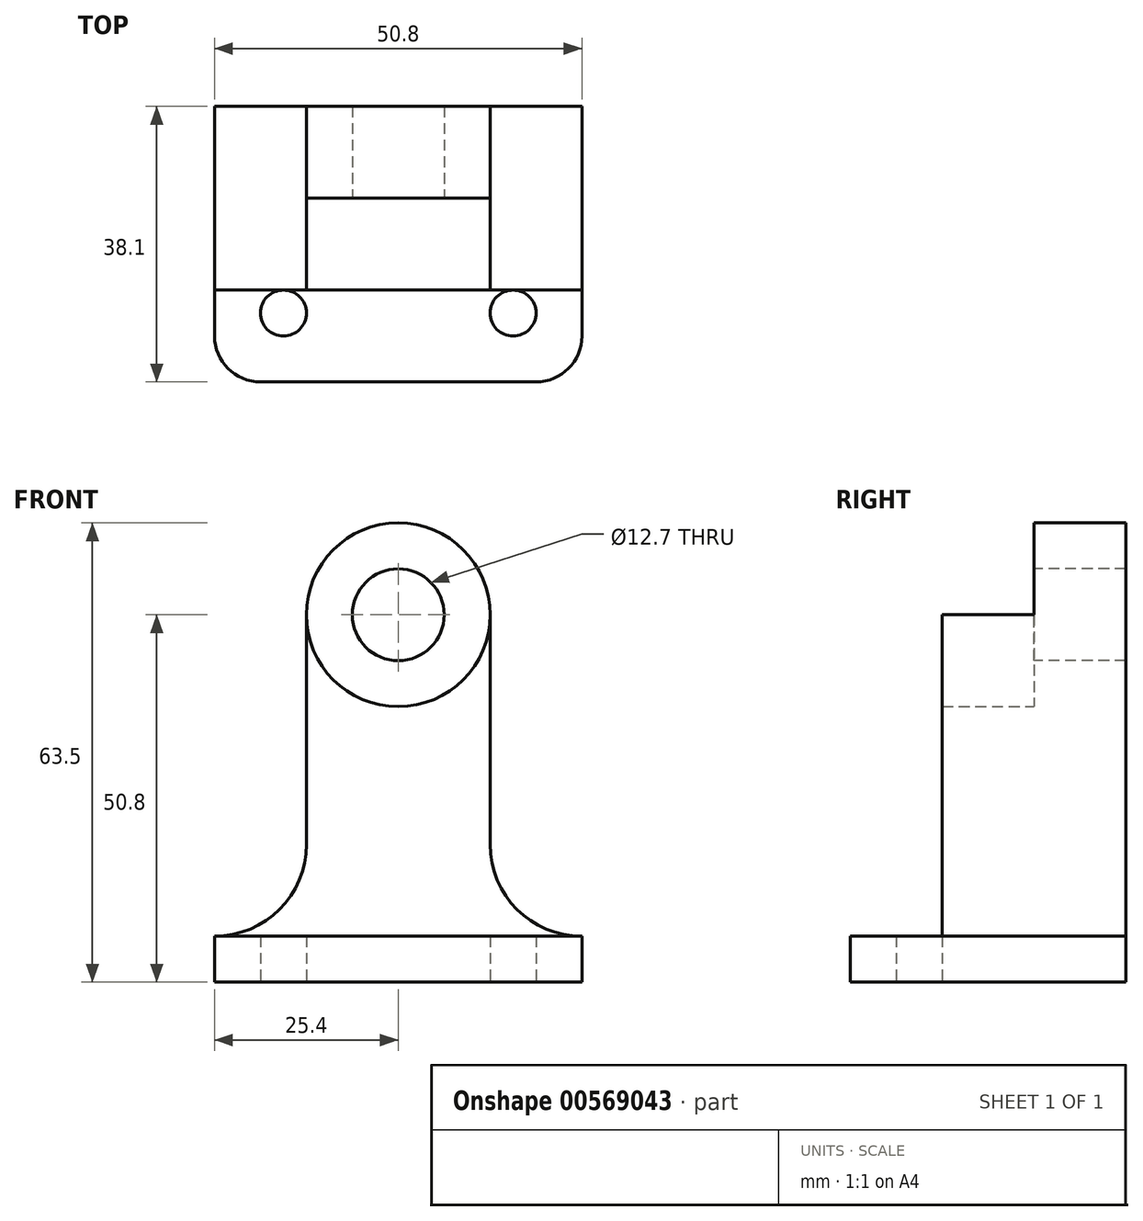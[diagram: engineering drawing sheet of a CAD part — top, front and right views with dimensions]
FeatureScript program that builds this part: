
annotation { "Feature Type Name" : "Feature", "Feature Type Description" : "" }
export const myFeature = defineFeature(function(context is Context, id is Id, definition is map)
    precondition{}
    {
        {
            var Q0;
            Q0=qCreatedBy(makeId("Top.planeOp"),FACE);
            var sketch = newSketch(context, id + "F0", { "sketchPlane" : qUnion([Q0])});
            skLineSegment(sketch, "E0", {"start": v(6.35, 0) * mm, "end": v(44.45, 0) * mm});
            skLineSegment(sketch, "E1", {"start": v(0, 6.35) * mm, "end": v(0, 38.1) * mm});
            skLineSegment(sketch, "E2", {"start": v(0, 38.1) * mm, "end": v(50.8, 38.1) * mm});
            skLineSegment(sketch, "E3", {"start": v(50.8, 38.1) * mm, "end": v(50.8, 6.35) * mm});
            skPoint(sketch, "E4.visualSharp", {"position": v(50.8, 0) * mm});
            skArc(sketch, "E4.filletArc", {"start": v(44.45, 0) * mm, "mid": v(48.94, 1.86) * mm, "end": v(50.8, 6.35) * mm});
            skCircle(sketch, "E5", {"center": v(9.52, 9.53) * mm, "radius": 3.18 * mm});
            skCircle(sketch, "E6", {"center": v(41.28, 9.53) * mm, "radius": 3.18 * mm});
            skPoint(sketch, "E7.visualSharp", {"position": v(0, 0) * mm});
            skArc(sketch, "E7.filletArc", {"start": v(0, 6.35) * mm, "mid": v(1.86, 1.86) * mm, "end": v(6.35, 0) * mm});
            skSolve(sketch);
        }
        {
            var Q0;
            Q0=makeQuery(id+"F0.imprint","IMPRINT",FACE,{"disambiguationData":[TD([[makeQuery(id+"F0.imprint","IMPRINT",EDGE,{"derivedFrom":sQuery(id+"F0.wireOp",EDGE,"E0")}),1.0]])]});
            extrude(context, id + "F1", {"entities" : qUnion([Q0]), "depth" : 6.35 * mm, "offsetDistance" : 25.4 * mm});
        }
        {
            var Q0;
            Q0=makeQuery(id+"F1.opExtrude","SWEPT_FACE",FACE,{"disambiguationData":[OSD([sQuery(id+"F0.wireOp",EDGE,"E2")])]});
            var sketch = newSketch(context, id + "F2", { "sketchPlane" : qUnion([Q0])});
            skLineSegment(sketch, "E8", {"start": v(-12.7, 19.05) * mm, "end": v(-12.7, 50.8) * mm});
            skLineSegment(sketch, "E9", {"start": v(-38.1, 19.05) * mm, "end": v(-38.1, 50.8) * mm});
            skArc(sketch, "E10", {"start": v(-50.8, 6.35) * mm, "mid": v(-41.82, 10.07) * mm, "end": v(-38.1, 19.05) * mm});
            skArc(sketch, "E11", {"start": v(-12.7, 19.05) * mm, "mid": v(-8.98, 10.07) * mm, "end": v(0, 6.35) * mm});
            skArc(sketch, "E12", {"start": v(-12.7, 50.8) * mm, "mid": v(-25.4, 63.5) * mm, "end": v(-38.1, 50.8) * mm});
            skSolve(sketch);
        }
        {
            var Q0;
            Q0 = qSketchRegion(id + "F2", true);
            var Q1;
            Q1=makeQuery(id+"F2.imprint","IMPRINT",FACE,{"disambiguationData":[TD([[makeQuery(id+"F2.imprint","IMPRINT",EDGE,{"derivedFrom":sQuery(id+"F2.wireOp",EDGE,"E8")}),1.0]])]});
            extrude(context, id + "F3", {"entities" : qUnion([Q0, Q1]), "operationType" : NewBodyOperationType.ADD, "oppositeDirection" : true, "depth" : 12.7 * mm, "offsetDistance" : 25.4 * mm});
        }
        {
            var Q0;
            Q0=makeQuery(id+"F3.opExtrude","CAP_FACE",FACE,{"disambiguationData":[OSD([sQuery(id+"F0.wireOp",EDGE,"E2"),sQuery(id+"F2.wireOp",EDGE,"E8"),sQuery(id+"F2.wireOp",EDGE,"E9"),sQuery(id+"F2.wireOp",EDGE,"E10"),sQuery(id+"F2.wireOp",EDGE,"E11"),sQuery(id+"F2.wireOp",EDGE,"E12")])],"isStart":false});
            var sketch = newSketch(context, id + "F4", { "sketchPlane" : qUnion([Q0])});
            skCircle(sketch, "E13", {"center": v(25.4, 50.8) * mm, "radius": 12.7 * mm});
            skCircle(sketch, "E14", {"center": v(25.4, 50.8) * mm, "radius": 6.35 * mm});
            skSolve(sketch);
        }
        {
            var Q0;
            Q0=makeQuery(id+"F4.imprint","IMPRINT",FACE,{"disambiguationData":[TD([[makeQuery(id+"F4.imprint","IMPRINT",EDGE,{"derivedFrom":sQuery(id+"F4.wireOp",EDGE,"E14")}),1.0]])]});
            extrude(context, id + "F5", {"entities" : qUnion([Q0]), "operationType" : NewBodyOperationType.REMOVE, "oppositeDirection" : true, "depth" : 25.4 * mm, "offsetDistance" : 25.4 * mm});
        }
        {
            var Q0;
            Q0=makeQuery(id+"F3.opExtrude","CAP_FACE",FACE,{"disambiguationData":[OSD([sQuery(id+"F0.wireOp",EDGE,"E2"),sQuery(id+"F2.wireOp",EDGE,"E8"),sQuery(id+"F2.wireOp",EDGE,"E9"),sQuery(id+"F2.wireOp",EDGE,"E10"),sQuery(id+"F2.wireOp",EDGE,"E11"),sQuery(id+"F2.wireOp",EDGE,"E12")])],"isStart":false});
            var sketch = newSketch(context, id + "F6", { "sketchPlane" : qUnion([Q0])});
            skCircle(sketch, "E15", {"center": v(25.4, 50.8) * mm, "radius": 12.7 * mm});
            skSolve(sketch);
        }
        {
            var Q0;
            {var subQ0=sQuery(id+"F6.wireOp",EDGE,"E15");Q0=makeQuery(id+"F6.imprint","IMPRINT",FACE,{"disambiguationData":[TD([[makeQuery(id+"F6.imprint","IMPRINT",EDGE,{"disambiguationData":[OD(0.0)],"derivedFrom":subQ0}),-1.0]])]});}
            extrude(context, id + "F7", {"entities" : qUnion([Q0]), "operationType" : NewBodyOperationType.ADD, "depth" : 12.7 * mm, "offsetDistance" : 25.4 * mm});
        }
    });
